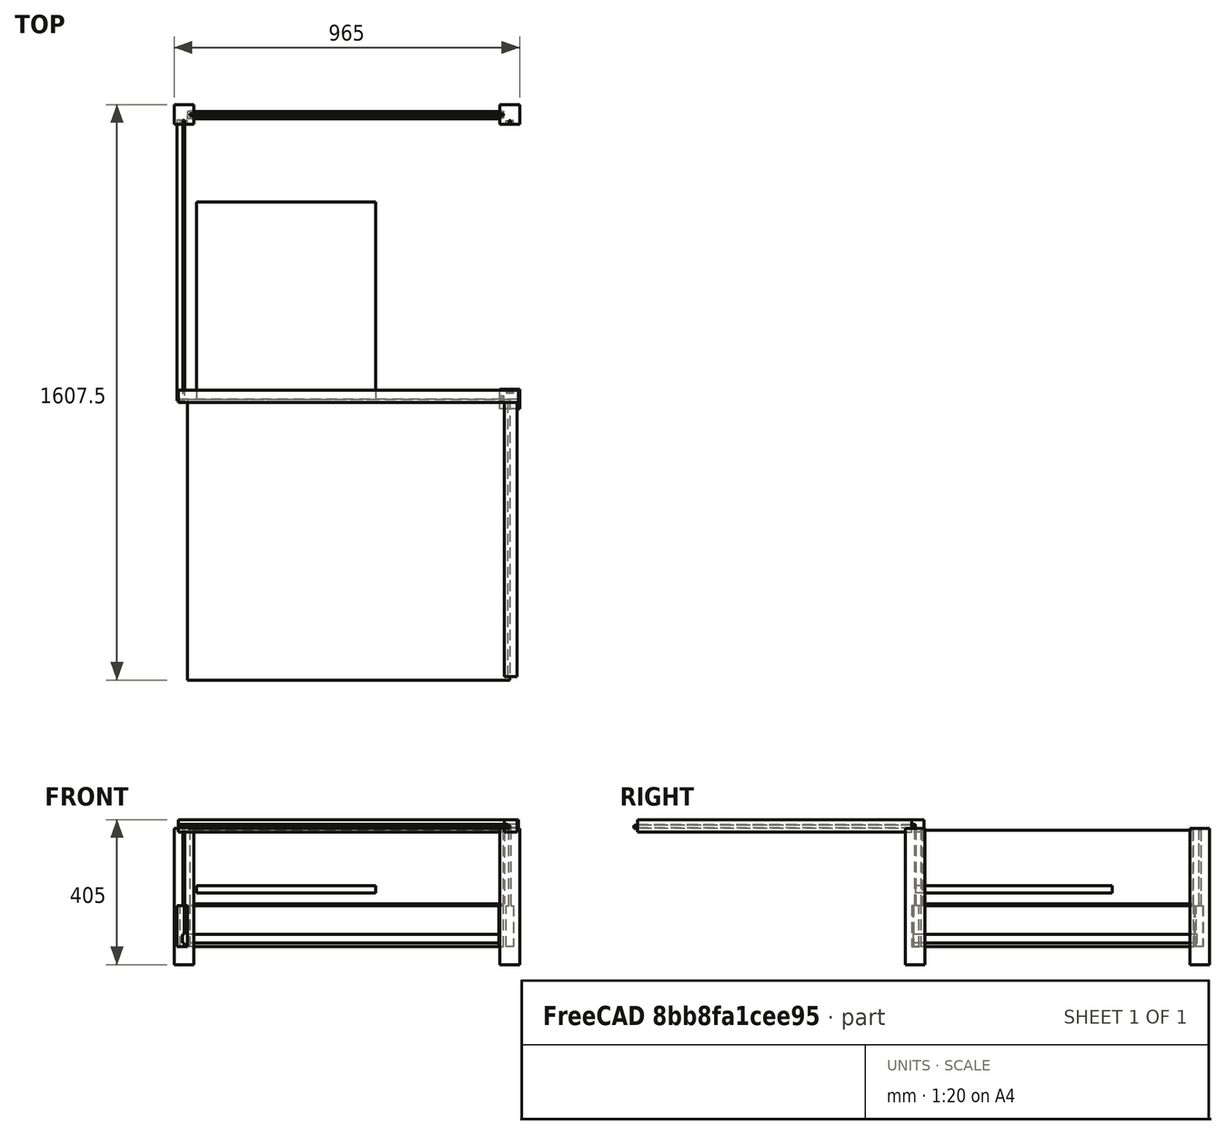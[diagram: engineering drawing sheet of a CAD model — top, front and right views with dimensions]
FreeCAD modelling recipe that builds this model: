
FCSTD DOCUMENT  (FreeCAD 0.19R22411 (Git))
Label: boitasemie
License: All rights reserved
LicenseURL: http://en.wikipedia.org/wiki/All_rights_reserved
objects: PartDesign::Body×18, TechDraw::DrawViewDimension×13, Sketcher::SketchObject×10, PartDesign::Pad×9, PartDesign::FeatureBase×9, TechDraw::DrawViewPart×5, TechDraw::DrawViewSection×5, App::DocumentObjectGroup×4, PartDesign::Plane×1, PartDesign::Pocket×1, PartDesign::PolarPattern×1, PartDesign::LinearPattern×1, App::Part×1, TechDraw::DrawSVGTemplate×1, TechDraw::DrawViewSymbol×1, TechDraw::DrawPage×1
note: 60 computed .brp shape members not serialized (recipe doc carries the construction recipe); baked Part::Feature solids carry a one-line shape summary decoded from their .brp

FEATURE [Sketcher::SketchObject] Sketch
  MapMode = 5
  Support = -> [XY_Plane]
  sketch-geometry (4):
    g0: LineSegment StartX=-27.5 StartY=27.5 StartZ=0 EndX=27.5 EndY=27.5 EndZ=0
    g1: LineSegment StartX=27.5 StartY=27.5 StartZ=0 EndX=27.5 EndY=-27.5 EndZ=0
    g2: LineSegment StartX=27.5 StartY=-27.5 StartZ=0 EndX=-27.5 EndY=-27.5 EndZ=0
    g3: LineSegment StartX=-27.5 StartY=-27.5 StartZ=0 EndX=-27.5 EndY=27.5 EndZ=0
  constraints (10):
    c: Coincident(g0,g1)
    c: Coincident(g2,g3)
    c: Coincident(g3,g0)
    c: Horizontal(g2)
    c: Vertical(g1)
    c: DistanceX(g0,g0) = 55
    c: DistanceY(g1,g1) = 55
    c: Coincident(g2,g1)
    c: Symmetric(g0,g2,g-1)
    c: Symmetric(g0,g0,g-2)
FEATURE [PartDesign::Pad] Pad
  AllowMultiFace = false
  Length = 380
  Length2 = 100
  Profile = -> Sketch
  Type = 0
FEATURE [PartDesign::Plane] DatumPlane
  Length = 2964
  MapMode = 5
  Placement = pos=(27.5,0,0) rot=(0.57735,0.57735,0.57735;2.0944rad)
  ResizeMode = 0
  Support = -> [Pad]
  Width = 2964
FEATURE [Sketcher::SketchObject] Sketch001  label="Fentespieds"
  MapMode = 5
  Placement = pos=(27.5,0,0) rot=(0.57735,0.57735,0.57735;2.0944rad)
  Support = -> [DatumPlane]
  sketch-geometry (8):
    g0: LineSegment StartX=-10 StartY=165 StartZ=0 EndX=-2.5 EndY=165 EndZ=0
    g1: LineSegment StartX=10 StartY=165 StartZ=0 EndX=10 EndY=50 EndZ=0
    g2: LineSegment StartX=10 StartY=50 StartZ=0 EndX=-10 EndY=50 EndZ=0
    g3: LineSegment StartX=-10 StartY=50 StartZ=0 EndX=-10 EndY=165 EndZ=0
    g4: LineSegment StartX=-2.5 StartY=510 StartZ=0 EndX=2.5 EndY=510 EndZ=0
    g5: LineSegment StartX=2.5 StartY=510 StartZ=0 EndX=2.5 EndY=165 EndZ=0
    g6: LineSegment StartX=-2.5 StartY=165 StartZ=0 EndX=-2.5 EndY=510 EndZ=0
    g7: LineSegment StartX=2.5 StartY=165 StartZ=0 EndX=10 EndY=165 EndZ=0
  constraints (20):
    c: Coincident(g7,g1)
    c: Coincident(g1,g2)
    c: Coincident(g2,g3)
    c: Coincident(g3,g0)
    c: Horizontal(g0)
    c: Vertical(g1)
    c: Vertical(g3)
    c: DistanceX(g2,g2) = 20
    c: Coincident(g4,g5)
    c: Coincident(g6,g4)
    c: Vertical(g5)
    c: Vertical(g6)
    c: DistanceX(g4,g4) = 5
    c: DistanceY(g-1,g2) = 50
    c: Symmetric(g2,g1,g-2)
    c: Symmetric(g4,g4,g-2)
    c: Coincident(g7,g5)
    c: Tangent(g0,g7)
    c: DistanceY(g1,g1) = 115
    c: Coincident(g6,g0)
FEATURE [PartDesign::Pocket] Pocket
  AllowMultiFace = false
  BaseFeature = -> Pad
  Length = 10
  Length2 = 100
  Profile = -> Sketch001
  Type = 0
FEATURE [PartDesign::PolarPattern] PolarPattern
  Angle = 90
  Axis = -> Z_Axis
  BaseFeature = -> Pocket
  Occurrences = 2
  Originals = -> [Pocket]
FEATURE [PartDesign::Body] Body  label="pieds1"
  Group = -> [Sketch,Sketch001,Pad,Pocket,PolarPattern]
  Origin = -> Origin
  Placement = pos=(-10,0,0) rot=(0,0,1;0rad)
  Tip = -> PolarPattern
FEATURE [PartDesign::FeatureBase] Clone
  BaseFeature = -> Body
FEATURE [PartDesign::Body] Body001  label="pieds2"
  BaseFeature = -> Body
  Group = -> [Clone]
  Origin = -> Origin001
  Placement = pos=(900,0,0) rot=(0,0,1;1.5708rad)
  Tip = -> Clone
FEATURE [PartDesign::FeatureBase] Clone002
  BaseFeature = -> Body
FEATURE [PartDesign::Body] Body003  label="pieds4"
  BaseFeature = -> Body
  Group = -> [Clone002]
  Origin = -> Origin003
  Placement = pos=(900,795,0) rot=(0,0,1;3.14159rad)
  Tip = -> Clone002
FEATURE [Sketcher::SketchObject] Sketch003
  AttachmentOffset = pos=(25,200,-550) rot=(0,0,1;0rad)
  MapMode = 5
  Placement = pos=(25,550,200) rot=(1,0,0;1.5708rad)
  Support = -> [XZ_Plane004]
  sketch-geometry (4):
    g0: LineSegment StartX=0 StartY=0 StartZ=0 EndX=150 EndY=0 EndZ=0
    g1: LineSegment StartX=150 StartY=0 StartZ=0 EndX=150 EndY=21 EndZ=0
    g2: LineSegment StartX=150 StartY=21 StartZ=0 EndX=0 EndY=21 EndZ=0
    g3: LineSegment StartX=0 StartY=21 StartZ=0 EndX=0 EndY=0 EndZ=0
  constraints (11):
    c: Coincident(g0,g1)
    c: Coincident(g1,g2)
    c: Coincident(g2,g3)
    c: Coincident(g3,g0)
    c: Horizontal(g0)
    c: Horizontal(g2)
    c: Vertical(g1)
    c: Vertical(g3)
    c: Coincident(g0,g-1)
    c: DistanceX(g0,g0) = 150
    c: DistanceY(g1,g1) = 21
FEATURE [PartDesign::Pad] Pad002
  AllowMultiFace = false
  Length = 550
  Length2 = 100
  Placement = pos=(0,0,0) rot=(1,0,0;1.5708rad)
  Profile = -> Sketch003
  Type = 0
FEATURE [PartDesign::LinearPattern] LinearPattern
  BaseFeature = -> Pad002
  Direction = -> Sketch003 [H_Axis]
  Length = 350
  Occurrences = 4
  Originals = -> [Pad002]
  Placement = pos=(0,0,0) rot=(1,0,0;1.5708rad)
FEATURE [PartDesign::Body] Body004  label="plancher"
  Group = -> [Sketch003,Pad002,LinearPattern]
  Origin = -> Origin004
  Tip = -> LinearPattern
FEATURE [Sketcher::SketchObject] Sketch007
  AttachmentOffset = pos=(-25,290,0) rot=(0,0,1;0rad)
  MapMode = 5
  Placement = pos=(-6.99e-14,-25,290) rot=(0.57735,0.57735,0.57735;2.0944rad)
  Support = -> [YZ_Plane005]
  sketch-geometry (4):
    g0: LineSegment StartX=-2.5 StartY=205 StartZ=0 EndX=2.5 EndY=205 EndZ=0
    g1: LineSegment StartX=2.5 StartY=205 StartZ=0 EndX=2.5 EndY=0 EndZ=0
    g2: LineSegment StartX=2.5 StartY=0 StartZ=0 EndX=-2.5 EndY=0 EndZ=0
    g3: LineSegment StartX=-2.5 StartY=0 StartZ=0 EndX=-2.5 EndY=205 EndZ=0
  constraints (11):
    c: Coincident(g0,g1)
    c: Coincident(g1,g2)
    c: Coincident(g2,g3)
    c: Coincident(g3,g0)
    c: Horizontal(g0)
    c: Vertical(g1)
    c: Vertical(g3)
    c: PointOnObject(g1,g-1)
    c: DistanceY(g1,g1) = 205
    c: DistanceX(g0,g0) = 5
    c: Symmetric(g1,g2,g-2)
FEATURE [PartDesign::Pad] Pad005
  AllowMultiFace = false
  Length = 755
  Length2 = 100
  Placement = pos=(0,0,0) rot=(0.57735,0.57735,0.57735;2.0944rad)
  Profile = -> Sketch007
  Type = 0
FEATURE [PartDesign::Body] Body005  label="vite laterale largeur 1"
  Group = -> [Sketch007,Pad005]
  Origin = -> Origin005
  Placement = pos=(875,20,-120) rot=(0,0,1;1.5708rad)
  Tip = -> Pad005
FEATURE [PartDesign::FeatureBase] Clone004
  BaseFeature = -> Body005
  Placement = pos=(0,25,0) rot=(0,0,1;0rad)
FEATURE [PartDesign::Body] Body007  label="vitre laterale largeur 2"
  BaseFeature = -> Body005
  Group = -> [Clone004]
  Origin = -> Origin007
  Placement = pos=(-10,20,-120) rot=(0,0,1;1.5708rad)
  Tip = -> Clone004
FEATURE [Sketcher::SketchObject] Sketch008
  MapMode = 5
  Placement = pos=(0,0,0) rot=(1,0,0;1.5708rad)
  Support = -> [XZ_Plane010]
  sketch-geometry (4):
    g0: LineSegment StartX=0 StartY=0 StartZ=0 EndX=900 EndY=0 EndZ=0
    g1: LineSegment StartX=900 StartY=0 StartZ=0 EndX=900 EndY=10 EndZ=0
    g2: LineSegment StartX=900 StartY=10 StartZ=0 EndX=0 EndY=10 EndZ=0
    g3: LineSegment StartX=0 StartY=10 StartZ=0 EndX=0 EndY=0 EndZ=0
  constraints (11):
    c: Coincident(g0,g1)
    c: Coincident(g1,g2)
    c: Coincident(g2,g3)
    c: Coincident(g3,g0)
    c: Horizontal(g0)
    c: Horizontal(g2)
    c: Vertical(g1)
    c: Vertical(g3)
    c: Coincident(g0,g-1)
    c: DistanceY(g1,g1) = 10
    c: DistanceX(g0,g0) = 900
FEATURE [PartDesign::Pad] Pad006
  AllowMultiFace = false
  Length = 785
  Length2 = 100
  Placement = pos=(0,0,0) rot=(1,0,0;1.5708rad)
  Profile = -> Sketch008
  Type = 0
FEATURE [PartDesign::Body] Body010  label="vitre couvercle"
  Group = -> [Sketch008,Pad006]
  Origin = -> Origin010
  Placement = pos=(0,0,380) rot=(1,0,0;0rad)
  Tip = -> Pad006
FEATURE [Sketcher::SketchObject] Sketch009
  AttachmentOffset = pos=(0,0,0) rot=(0,1,0;1.5708rad)
  MapMode = 5
  Placement = pos=(0,0,0) rot=(0.57735,0.57735,0.57735;2.0944rad)
  Support = -> [XZ_Plane011]
  sketch-geometry (8):
    g0: LineSegment StartX=31.4867 StartY=50 StartZ=0 EndX=52.4867 EndY=50 EndZ=0
    g1: LineSegment StartX=52.4867 StartY=50 StartZ=0 EndX=52.4867 EndY=60 EndZ=0
    g2: LineSegment StartX=52.4867 StartY=60 StartZ=0 EndX=47.4867 EndY=60 EndZ=0
    g3: LineSegment StartX=47.4867 StartY=60 StartZ=0 EndX=47.4867 EndY=85 EndZ=0
    g4: LineSegment StartX=47.4867 StartY=85 StartZ=0 EndX=52.4867 EndY=85 EndZ=0
    g5: LineSegment StartX=52.4867 StartY=85 StartZ=0 EndX=52.4867 EndY=165 EndZ=0
    g6: LineSegment StartX=52.4867 StartY=165 StartZ=0 EndX=31.4867 EndY=165 EndZ=0
    g7: LineSegment StartX=31.4867 StartY=165 StartZ=0 EndX=31.4867 EndY=50 EndZ=0
  constraints (23):
    c: Vertical(g1)
    c: Coincident(g1,g2)
    c: Horizontal(g2)
    c: Coincident(g2,g3)
    c: Vertical(g3)
    c: Coincident(g3,g4)
    c: Horizontal(g4)
    c: Coincident(g4,g5)
    c: Vertical(g5)
    c: Coincident(g5,g6)
    c: Horizontal(g6)
    c: Coincident(g6,g7)
    c: Vertical(g7)
    c: DistanceY(g7,g7) = 115
    c: DistanceY(g3,g3) = 25
    c: DistanceY(g0,g1) = 10
    c: DistanceX(g4,g4) = 5
    c: DistanceX(g6,g6) = 21
    c: Equal(g6,g0)
    c: Coincident(g0,g1)
    c: Horizontal(g0)
    c: Coincident(g7,g0)
    c: DistanceY(g-1,g0) = 50
FEATURE [PartDesign::Pad] Pad008
  AllowMultiFace = false
  Length = 870
  Length2 = 100
  Placement = pos=(0,0,0) rot=(1,0,0;1.5708rad)
  Profile = -> Sketch009
  Type = 0
FEATURE [PartDesign::Body] Body011  label="largeur1"
  Group = -> [Pad008,Sketch009]
  Origin = -> Origin011
  Placement = pos=(0,-42,0) rot=(0,0,1;0rad)
  Tip = -> Pad008
FEATURE [PartDesign::FeatureBase] Clone007
  BaseFeature = -> Body011
FEATURE [PartDesign::Body] Body012  label="largeur2"
  BaseFeature = -> Body011
  Group = -> [Clone007]
  Origin = -> Origin012
  Placement = pos=(870,835,0) rot=(0,0,1;3.14159rad)
  Tip = -> Clone007
FEATURE [Sketcher::SketchObject] Sketch010
  AttachmentOffset = pos=(0,0,0) rot=(0,1,0;1.5708rad)
  MapMode = 5
  Placement = pos=(0,0,0) rot=(0.57735,0.57735,0.57735;2.0944rad)
  Support = -> [XZ_Plane014]
  sketch-geometry (8):
    g0: LineSegment StartX=0.0345758 StartY=50 StartZ=0 EndX=21.0346 EndY=50 EndZ=0
    g1: LineSegment StartX=21.0346 StartY=50 StartZ=0 EndX=21.0346 EndY=60 EndZ=0
    g2: LineSegment StartX=21.0346 StartY=60 StartZ=0 EndX=16.0346 EndY=60 EndZ=0
    g3: LineSegment StartX=16.0346 StartY=60 StartZ=0 EndX=16.0346 EndY=85 EndZ=0
    g4: LineSegment StartX=16.0346 StartY=85 StartZ=0 EndX=21.0346 EndY=85 EndZ=0
    g5: LineSegment StartX=21.0346 StartY=85 StartZ=0 EndX=21.0346 EndY=165 EndZ=0
    g6: LineSegment StartX=21.0346 StartY=165 StartZ=0 EndX=0.0345758 EndY=165 EndZ=0
    g7: LineSegment StartX=0.0345758 StartY=165 StartZ=0 EndX=0.0345758 EndY=50 EndZ=0
  constraints (23):
    c: Coincident(g0,g1)
    c: Vertical(g1)
    c: Coincident(g1,g2)
    c: Horizontal(g2)
    c: Coincident(g2,g3)
    c: Vertical(g3)
    c: Coincident(g3,g4)
    c: Horizontal(g4)
    c: Coincident(g4,g5)
    c: Vertical(g5)
    c: Coincident(g5,g6)
    c: Horizontal(g6)
    c: Coincident(g6,g7)
    c: Vertical(g7)
    c: DistanceY(g7,g7) = 115
    c: DistanceY(g3,g3) = 25
    c: DistanceY(g0,g1) = 10
    c: DistanceX(g4,g4) = 5
    c: DistanceX(g6,g6) = 21
    c: Equal(g6,g0)
    c: Horizontal(g0)
    c: Coincident(g7,g0)
    c: DistanceY(g-1,g0) = 50
FEATURE [PartDesign::Pad] Pad009
  AllowMultiFace = false
  Length = 785
  Length2 = 100
  Placement = pos=(0,0,0) rot=(1,0,0;1.5708rad)
  Profile = -> Sketch010
  Type = 0
FEATURE [PartDesign::Body] Body013  label="longeur1"
  Group = -> [Pad009,Sketch010]
  Origin = -> Origin013
  Placement = pos=(910,20,0) rot=(0,0,1;1.5708rad)
  Tip = -> Pad009
FEATURE [PartDesign::FeatureBase] Clone008
  BaseFeature = -> Body013
  Placement = pos=(900,0,0) rot=(0,0,1;1.5708rad)
FEATURE [PartDesign::Body] Body014  label="longeur2"
  BaseFeature = -> Body013
  Group = -> [Clone008]
  Origin = -> Origin014
  Placement = pos=(870,780,0) rot=(0,0,1;3.14159rad)
  Tip = -> Clone008
FEATURE [PartDesign::FeatureBase] Clone009
  BaseFeature = -> Body
FEATURE [PartDesign::Body] Body015  label="pieds3"
  BaseFeature = -> Body
  Group = -> [Clone009]
  Origin = -> Origin015
  Placement = pos=(-10,795,0) rot=(0,0,-1;1.5708rad)
  Tip = -> Clone009
FEATURE [App::DocumentObjectGroup] Group  label="Pieds"
  Group = -> [Body,Body001,Body003,Body015]
FEATURE [Sketcher::SketchObject] Sketch011
  MapMode = 5
  Placement = pos=(0,0,0) rot=(1,0,0;1.5708rad)
  Support = -> [XZ_Plane017]
  sketch-geometry (8):
    g0: LineSegment StartX=0 StartY=0 StartZ=0 EndX=35 EndY=0 EndZ=0
    g1: LineSegment StartX=35 StartY=0 StartZ=0 EndX=35 EndY=12.5 EndZ=0
    g2: LineSegment StartX=35 StartY=35 StartZ=0 EndX=0 EndY=35 EndZ=0
    g3: LineSegment StartX=0 StartY=35 StartZ=0 EndX=0 EndY=0 EndZ=0
    g4: LineSegment StartX=35 StartY=22.5 StartZ=0 EndX=25 EndY=22.5 EndZ=0
    g5: LineSegment StartX=25 StartY=22.5 StartZ=0 EndX=25 EndY=12.5 EndZ=0
    g6: LineSegment StartX=25 StartY=12.5 StartZ=0 EndX=35 EndY=12.5 EndZ=0
    g7: LineSegment StartX=35 StartY=22.5 StartZ=0 EndX=35 EndY=35 EndZ=0
  constraints (23):
    c: Coincident(g0,g1)
    c: Coincident(g2,g3)
    c: Coincident(g3,g0)
    c: Horizontal(g0)
    c: Horizontal(g2)
    c: Vertical(g1)
    c: Vertical(g3)
    c: Coincident(g0,g-1)
    c: Horizontal(g4)
    c: Coincident(g4,g5)
    c: Vertical(g5)
    c: Coincident(g5,g6)
    c: Horizontal(g6)
    c: Coincident(g1,g6)
    c: Coincident(g7,g4)
    c: Vertical(g7)
    c: Coincident(g7,g2)
    c: DistanceX(g2,g2) = 35
    c: Equal(g2,g0)
    c: DistanceY(g3,g3) = 35
    c: DistanceY(g5,g5) = 10
    c: DistanceX(g6,g6) = 10
    c: DistanceY(g0,g1) = 12.5
FEATURE [PartDesign::Pad] Pad010
  AllowMultiFace = false
  Length = 765
  Length2 = 100
  Placement = pos=(0,0,0) rot=(1,0,0;1.5708rad)
  Profile = -> Sketch011
  Type = 0
FEATURE [PartDesign::Body] Body016  label="vitre couvercle largeur1 1"
  Group = -> [Sketch011,Pad010]
  Origin = -> Origin016
  Placement = pos=(-27,-10,370) rot=(0,0,1;0rad)
  Tip = -> Pad010
FEATURE [PartDesign::FeatureBase] Clone010
  BaseFeature = -> Body016
  Placement = pos=(-20,0,370) rot=(0,0,1;0rad)
FEATURE [PartDesign::Body] Body017  label="vitre couvercle largeur 2"
  BaseFeature = -> Body016
  Group = -> [Clone010]
  Origin = -> Origin017
  Placement = pos=(900,-775,0) rot=(0,0,1;3.14159rad)
  Tip = -> Clone010
FEATURE [Sketcher::SketchObject] Sketch012
  MapMode = 5
  Placement = pos=(0,0,0) rot=(1,0,0;1.5708rad)
  Support = -> [XZ_Plane019]
  sketch-geometry (8):
    g0: LineSegment StartX=0 StartY=0 StartZ=0 EndX=35 EndY=0 EndZ=0
    g1: LineSegment StartX=35 StartY=0 StartZ=0 EndX=35 EndY=12.5 EndZ=0
    g2: LineSegment StartX=35 StartY=35 StartZ=0 EndX=0 EndY=35 EndZ=0
    g3: LineSegment StartX=0 StartY=35 StartZ=0 EndX=0 EndY=0 EndZ=0
    g4: LineSegment StartX=35 StartY=22.5 StartZ=0 EndX=25 EndY=22.5 EndZ=0
    g5: LineSegment StartX=25 StartY=22.5 StartZ=0 EndX=25 EndY=12.5 EndZ=0
    g6: LineSegment StartX=25 StartY=12.5 StartZ=0 EndX=35 EndY=12.5 EndZ=0
    g7: LineSegment StartX=35 StartY=22.5 StartZ=0 EndX=35 EndY=35 EndZ=0
  constraints (22):
    c: Coincident(g0,g1)
    c: Coincident(g7,g2)
    c: Coincident(g2,g3)
    c: Coincident(g3,g0)
    c: Horizontal(g0)
    c: Horizontal(g2)
    c: Vertical(g1)
    c: Vertical(g3)
    c: Coincident(g0,g-1)
    c: DistanceY(g1,g7) = 35
    c: DistanceX(g2,g2) = 35
    c: Horizontal(g4)
    c: Coincident(g4,g5)
    c: Coincident(g5,g6)
    c: Horizontal(g6)
    c: Vertical(g5)
    c: Coincident(g1,g6)
    c: Coincident(g7,g4)
    c: Tangent(g1,g7)
    c: DistanceX(g4,g4) = 10
    c: DistanceY(g5,g5) = 10
    c: DistanceY(g1,g1) = 12.5
FEATURE [PartDesign::Pad] Pad011
  AllowMultiFace = false
  Length = 950
  Length2 = 100
  Placement = pos=(0,0,0) rot=(1,0,0;1.5708rad)
  Profile = -> Sketch012
  Type = 0
FEATURE [PartDesign::Body] Body018  label="vitre couvercle longeur 1"
  Group = -> [Sketch012,Pad011]
  Origin = -> Origin018
  Placement = pos=(-30,-810,370) rot=(0,0,1;1.5708rad)
  Tip = -> Pad011
FEATURE [PartDesign::FeatureBase] Clone011
  BaseFeature = -> Body018
  Placement = pos=(-30,-810,370) rot=(0,0,1;1.5708rad)
FEATURE [PartDesign::Body] Body019  label="vitre couvercle longeur 2"
  BaseFeature = -> Body018
  Group = -> [Clone011]
  Origin = -> Origin019
  Placement = pos=(894,-785,0) rot=(0,0,1;3.14159rad)
  Tip = -> Clone011
FEATURE [App::DocumentObjectGroup] Group003  label="couvercle"
  Group = -> [Body010,Body016,Body017,Body018,Body019]
FEATURE [App::Part] Part
  Group = -> [Body010,Body016,Body019,Body018,Body017,Group003]
  Origin = -> Origin020
  Placement = pos=(-10,610,90) rot=(1,0,0;-0.523599rad)
FEATURE [Sketcher::SketchObject] Sketch013
  AttachmentOffset = pos=(-25,290,0) rot=(0,0,1;0rad)
  MapMode = 5
  Placement = pos=(-6.99e-14,-25,290) rot=(0.57735,0.57735,0.57735;2.0944rad)
  Support = -> [YZ_Plane008]
  sketch-geometry (4):
    g0: LineSegment StartX=-2.5 StartY=205 StartZ=0 EndX=2.5 EndY=205 EndZ=0
    g1: LineSegment StartX=2.5 StartY=205 StartZ=0 EndX=2.5 EndY=0 EndZ=0
    g2: LineSegment StartX=2.5 StartY=0 StartZ=0 EndX=-2.5 EndY=0 EndZ=0
    g3: LineSegment StartX=-2.5 StartY=0 StartZ=0 EndX=-2.5 EndY=205 EndZ=0
  constraints (11):
    c: Coincident(g0,g1)
    c: Coincident(g1,g2)
    c: Coincident(g2,g3)
    c: Coincident(g3,g0)
    c: Horizontal(g0)
    c: Vertical(g1)
    c: Vertical(g3)
    c: PointOnObject(g1,g-1)
    c: DistanceY(g1,g1) = 205
    c: DistanceX(g0,g0) = 5
    c: Symmetric(g1,g2,g-2)
FEATURE [PartDesign::Pad] Pad012
  AllowMultiFace = false
  Length = 870
  Length2 = 100
  Placement = pos=(0,0,0) rot=(0.57735,0.57735,0.57735;2.0944rad)
  Profile = -> Sketch013
  Type = 0
FEATURE [PartDesign::Body] Body008  label="vitre laterale longeur 1"
  Group = -> [Pad012,Sketch013]
  Origin = -> Origin008
  Placement = pos=(10,25,-120) rot=(0,0,1;0rad)
  Tip = -> Pad012
FEATURE [PartDesign::FeatureBase] Clone012
  BaseFeature = -> Body008
  Placement = pos=(-15,35,-120) rot=(0,0,1;0rad)
FEATURE [PartDesign::Body] Body020  label="vitre laterale longeur 2"
  BaseFeature = -> Body008
  Group = -> [Clone012]
  Origin = -> Origin021
  Placement = pos=(30,785,0) rot=(0,0,1;0rad)
  Tip = -> Clone012
FEATURE [App::DocumentObjectGroup] Group001  label="vitres laterales"
  Group = -> [Body005,Body007,Body008,Body020]
FEATURE [App::DocumentObjectGroup] Group002  label="laterale"
  Group = -> [Body011,Body012,Body013,Body014,Group001]
FEATURE [TechDraw::DrawSVGTemplate] Template
  EditableTexts = Designed_by_Name=Designed by Name; Drawing_number=Drawing number; FC-Date=Date; FC-SC=Scale; FC-SH=Sheet; FC-Title=Title; Subtitle=Subtitle; Weight=Weight
  Height = 210
  Orientation = 1
  Width = 297
FEATURE [TechDraw::DrawViewPart] View  label="pieds"
  CoarseView = false
  Direction = (1,0,0)
  Focus = 100
  HardHidden = false
  IsoCount = 0
  IsoHidden = false
  IsoVisible = false
  LockPosition = false
  Perspective = false
  Rotation = 0
  Scale = 0.1
  ScaleType = 0
  SeamHidden = false
  SeamVisible = true
  SmoothHidden = false
  SmoothVisible = true
  Source = -> [Body]
  X = 32.6298
  XDirection = (0,1,0)
  Y = 162.427
FEATURE [TechDraw::DrawViewSection] SectionView  label="Section  - pieds"
  BaseView = -> View
  CoarseView = false
  CutSurfaceDisplay = 2
  Direction = (0,0,1)
  FileGeomPattern = <path>
  FileHatchPattern = <path>
  Focus = 100
  FuseBeforeCut = false
  HardHidden = false
  HatchScale = 1
  IsoCount = 0
  IsoHidden = false
  IsoVisible = false
  LockPosition = false
  NameGeomPattern = Diamond
  Perspective = false
  Rotation = 0
  Scale = 0.1
  ScaleType = 0
  SeamHidden = false
  SeamVisible = true
  SectionDirection = 3
  SectionNormal = (0,0,1)
  SectionOrigin = (0,0,110)
  SmoothHidden = false
  SmoothVisible = true
  Source = -> [Body]
  X = 32.6103
  XDirection = (0,1,0)
  Y = 136.958
FEATURE [TechDraw::DrawViewPart] View001
  CoarseView = false
  Direction = (0,-1,0)
  Focus = 100
  HardHidden = false
  IsoCount = 0
  IsoHidden = false
  IsoVisible = false
  LockPosition = false
  Perspective = false
  Rotation = 0
  Scale = 0.1
  ScaleType = 0
  SeamHidden = false
  SeamVisible = true
  SmoothHidden = false
  SmoothVisible = true
  Source = -> [Body011]
  X = 222.063
  XDirection = (1,0,0)
  Y = 156.673
FEATURE [TechDraw::DrawViewSection] SectionView001  label="Section  - "
  BaseView = -> View001
  CoarseView = false
  CutSurfaceDisplay = 2
  Direction = (-1,0,0)
  FileGeomPattern = <path>
  FileHatchPattern = <path>
  Focus = 100
  FuseBeforeCut = false
  HardHidden = false
  HatchScale = 1
  IsoCount = 0
  IsoHidden = false
  IsoVisible = false
  LockPosition = false
  NameGeomPattern = Diamond
  Perspective = false
  Rotation = 0
  Scale = 0.1
  ScaleType = 0
  SeamHidden = false
  SeamVisible = true
  SectionDirection = 0
  SectionNormal = (-1,0,0)
  SectionOrigin = (450,2,107.5)
  SmoothHidden = false
  SmoothVisible = true
  Source = -> [Body011]
  X = 275.235
  XDirection = (0,-1,0)
  Y = 156.051
FEATURE [TechDraw::DrawViewPart] View002
  CoarseView = false
  Direction = (1,0,0)
  Focus = 100
  HardHidden = false
  IsoCount = 0
  IsoHidden = false
  IsoVisible = false
  LockPosition = false
  Perspective = false
  Rotation = 0
  Scale = 0.1
  ScaleType = 0
  SeamHidden = false
  SeamVisible = true
  SmoothHidden = false
  SmoothVisible = true
  Source = -> [Body013]
  X = 217.796
  XDirection = (0,1,0)
  Y = 131.734
FEATURE [TechDraw::DrawViewSection] SectionView002  label="Section  - 001"
  BaseView = -> View002
  CoarseView = false
  CutSurfaceDisplay = 2
  Direction = (0,-1,0)
  FileGeomPattern = <path>
  FileHatchPattern = <path>
  Focus = 100
  FuseBeforeCut = false
  HardHidden = false
  HatchScale = 1
  IsoCount = 0
  IsoHidden = false
  IsoVisible = false
  LockPosition = false
  NameGeomPattern = Diamond
  Perspective = false
  Rotation = 0
  Scale = 0.1
  ScaleType = 0
  SeamHidden = false
  SeamVisible = true
  SectionDirection = 0
  SectionNormal = (0,-1,0)
  SectionOrigin = (894.5,392.5,107.5)
  SmoothHidden = false
  SmoothVisible = true
  Source = -> [Body013]
  X = 266.381
  XDirection = (1,0,0)
  Y = 130.961
FEATURE [TechDraw::DrawViewDimension] Dimension005
  Arbitrary = false
  FormatSpec = %.2f
  Inverted = false
  LockPosition = false
  MeasureType = 1
  OverTolerance = 0
  References2D = -> [View001]
  Rotation = 0
  Scale = 0.1
  ScaleType = 0
  TheoreticalExact = false
  Type = 1
  UnderTolerance = 0
  X = 1.01639
  Y = 17.6079
FEATURE [TechDraw::DrawViewDimension] Dimension006
  Arbitrary = false
  FormatSpec = %.2f
  Inverted = false
  LockPosition = false
  MeasureType = 1
  OverTolerance = 0
  References2D = -> [View002]
  Rotation = 0
  Scale = 0.1
  ScaleType = 0
  TheoreticalExact = false
  Type = 1
  UnderTolerance = 0
  X = 1.35519
  Y = 14.5587
FEATURE [TechDraw::DrawViewPart] View005
  CoarseView = false
  Direction = (1,0,0)
  Focus = 100
  HardHidden = false
  IsoCount = 0
  IsoHidden = false
  IsoVisible = false
  LockPosition = false
  Perspective = false
  Rotation = 0
  Scale = 0.1
  ScaleType = 0
  SeamHidden = false
  SeamVisible = true
  SmoothHidden = false
  SmoothVisible = true
  Source = -> [Pad010]
  X = 99.7668
  XDirection = (0,-1,0)
  Y = 134.759
FEATURE [TechDraw::DrawViewSection] SectionView005  label="Section  - 004"
  BaseView = -> View005
  CoarseView = false
  CutSurfaceDisplay = 2
  Direction = (0,1,0)
  FileGeomPattern = <path>
  FileHatchPattern = <path>
  Focus = 100
  FuseBeforeCut = false
  HardHidden = false
  HatchScale = 1
  IsoCount = 0
  IsoHidden = false
  IsoVisible = false
  LockPosition = false
  NameGeomPattern = Diamond
  Perspective = false
  Rotation = 0
  Scale = 0.1
  ScaleType = 0
  SeamHidden = false
  SeamVisible = true
  SectionDirection = 0
  SectionNormal = (0,1,0)
  SectionOrigin = (17.5,-382.5,17.5)
  SmoothHidden = false
  SmoothVisible = true
  Source = -> [Pad010]
  X = 148.89
  XDirection = (1,0,0)
  Y = 134.796
FEATURE [TechDraw::DrawViewDimension] Dimension
  Arbitrary = false
  FormatSpec = %.2f
  Inverted = false
  LockPosition = false
  MeasureType = 1
  OverTolerance = 0
  References2D = -> [View005]
  Rotation = 0
  Scale = 0.1
  ScaleType = 0
  TheoreticalExact = false
  Type = 1
  UnderTolerance = 0
  X = 0.518027
  Y = 10.8155
FEATURE [TechDraw::DrawViewDimension] Dimension007
  Arbitrary = false
  FormatSpec = %.2f
  Inverted = false
  LockPosition = false
  MeasureType = 1
  OverTolerance = 0
  References2D = -> [View]
  Rotation = 0
  Scale = 0.1
  ScaleType = 0
  TheoreticalExact = false
  Type = 2
  UnderTolerance = 0
  X = 13.5773
  Y = 2.04289
FEATURE [TechDraw::DrawViewDimension] Dimension008
  Arbitrary = false
  FormatSpec = %.2f
  Inverted = false
  LockPosition = false
  MeasureType = 1
  OverTolerance = 0
  References2D = -> [SectionView]
  Rotation = 0
  Scale = 0.1
  ScaleType = 0
  TheoreticalExact = false
  Type = 1
  UnderTolerance = 0
  X = -8.9511
  Y = -14.0386
FEATURE [TechDraw::DrawViewDimension] Dimension009
  Arbitrary = false
  FormatSpec = %.2f
  Inverted = false
  LockPosition = false
  MeasureType = 1
  OverTolerance = 0
  References2D = -> [View]
  Rotation = 0
  Scale = 0.1
  ScaleType = 0
  TheoreticalExact = false
  Type = 2
  UnderTolerance = 0
  X = -18.104
  Y = -8.91722
FEATURE [TechDraw::DrawViewDimension] Dimension010
  Arbitrary = false
  FormatSpec = %.2f
  Inverted = false
  LockPosition = false
  MeasureType = 1
  OverTolerance = 0
  References2D = -> [View]
  Rotation = 0
  Scale = 0.1
  ScaleType = 0
  TheoreticalExact = false
  Type = 2
  UnderTolerance = 0
  X = 4.64886
  Y = -1.80749
FEATURE [TechDraw::DrawViewDimension] Dimension011
  Arbitrary = false
  FormatSpec = %.2f
  Inverted = false
  LockPosition = false
  MeasureType = 1
  OverTolerance = 0
  References2D = -> [SectionView]
  Rotation = 0
  Scale = 0.1
  ScaleType = 0
  TheoreticalExact = false
  Type = 1
  UnderTolerance = 0
  X = 9.63526
  Y = -4.77171
FEATURE [TechDraw::DrawViewDimension] Dimension012
  Arbitrary = false
  FormatSpec = %.2f
  Inverted = false
  LockPosition = false
  MeasureType = 1
  OverTolerance = 0
  References2D = -> [View]
  Rotation = 0
  Scale = 0.1
  ScaleType = 0
  TheoreticalExact = false
  Type = 1
  UnderTolerance = 0
  X = -5.92939
  Y = 27.609
FEATURE [TechDraw::DrawViewDimension] Dimension013
  Arbitrary = false
  FormatSpec = %.2f
  Inverted = false
  LockPosition = false
  MeasureType = 1
  OverTolerance = 0
  References2D = -> [SectionView005]
  Rotation = 0
  Scale = 0.1
  ScaleType = 0
  TheoreticalExact = false
  Type = 1
  UnderTolerance = 0
  X = 9.95043
  Y = 11.7989
FEATURE [TechDraw::DrawViewDimension] Dimension014
  Arbitrary = false
  FormatSpec = %.2f
  Inverted = false
  LockPosition = false
  MeasureType = 1
  OverTolerance = 0
  References2D = -> [SectionView005]
  Rotation = 0
  Scale = 0.1
  ScaleType = 0
  TheoreticalExact = false
  Type = 2
  UnderTolerance = 0
  X = 13.3753
  Y = -9.95043
FEATURE [TechDraw::DrawViewSymbol] ActiveView001
  LockPosition = false
  Rotation = 0
  Scale = 0.5
  ScaleType = 2
  Symbol = <blob: 165818 chars omitted>
  X = 78.5064
  Y = 63.2359
FEATURE [TechDraw::DrawViewPart] View004
  CoarseView = false
  Direction = (0,1,-0.004)
  Focus = 100
  HardHidden = false
  IsoCount = 0
  IsoHidden = false
  IsoVisible = false
  LockPosition = false
  Perspective = false
  Rotation = 0
  Scale = 0.1
  ScaleType = 0
  SeamHidden = false
  SeamVisible = true
  SmoothHidden = false
  SmoothVisible = true
  Source = -> [Body018]
  X = 110.128
  XDirection = (-1,0,0.008)
  Y = 171.1
FEATURE [TechDraw::DrawViewDimension] Dimension004
  Arbitrary = false
  FormatSpec = %.2f
  Inverted = false
  LockPosition = false
  MeasureType = 1
  OverTolerance = 0
  References2D = -> [View004]
  Rotation = 0
  Scale = 0.1
  ScaleType = 0
  TheoreticalExact = false
  Type = 1
  UnderTolerance = 0
  X = 0.729977
  Y = 11.4219
FEATURE [TechDraw::DrawViewSection] SectionView004  label="Section  - 003"
  BaseView = -> View004
  CoarseView = false
  CutSurfaceDisplay = 2
  Direction = (0.999968,-3.19985e-05,-0.00799962)
  FileGeomPattern = <path>
  FileHatchPattern = <path>
  Focus = 100
  FuseBeforeCut = false
  HardHidden = false
  HatchScale = 1
  IsoCount = 0
  IsoHidden = false
  IsoVisible = false
  LockPosition = false
  NameGeomPattern = Diamond
  Perspective = false
  Rotation = 0
  Scale = 0.1
  ScaleType = 0
  SeamHidden = false
  SeamVisible = true
  SectionDirection = 0
  SectionNormal = (0.999968,-3.19985e-05,-0.00799962)
  SectionOrigin = (445,-792.5,387.5)
  SmoothHidden = false
  SmoothVisible = true
  Source = -> [Body018]
  X = 164.401
  XDirection = (0,0.999992,-0.00399997)
  Y = 170.845
FEATURE [TechDraw::DrawViewDimension] Dimension015
  Arbitrary = false
  FormatSpec = %.2f
  Inverted = false
  LockPosition = false
  MeasureType = 1
  OverTolerance = 0
  References2D = -> [SectionView]
  Rotation = 0
  Scale = 0.1
  ScaleType = 0
  TheoreticalExact = false
  Type = 2
  UnderTolerance = 0
  X = -13.3719
  Y = -3.9604
FEATURE [TechDraw::DrawPage] Page
  KeepUpdated = true
  NextBalloonIndex = 2
  ProjectionType = 0
  Scale = 0.1
  Template = -> Template
  Views = -> [View,SectionView,View001,SectionView001,View002,SectionView002,View004,Dimension004,SectionView004,Dimension005,Dimension006,View005,SectionView005,Dimension,Dimension007,Dimension008,Dimension009,Dimension010,Dimension011,Dimension012,Dimension013,Dimension014,ActiveView001,Dimension015]
note: 10 file-system paths scrubbed to <path> (originals preserved in the JSON sidecar)
